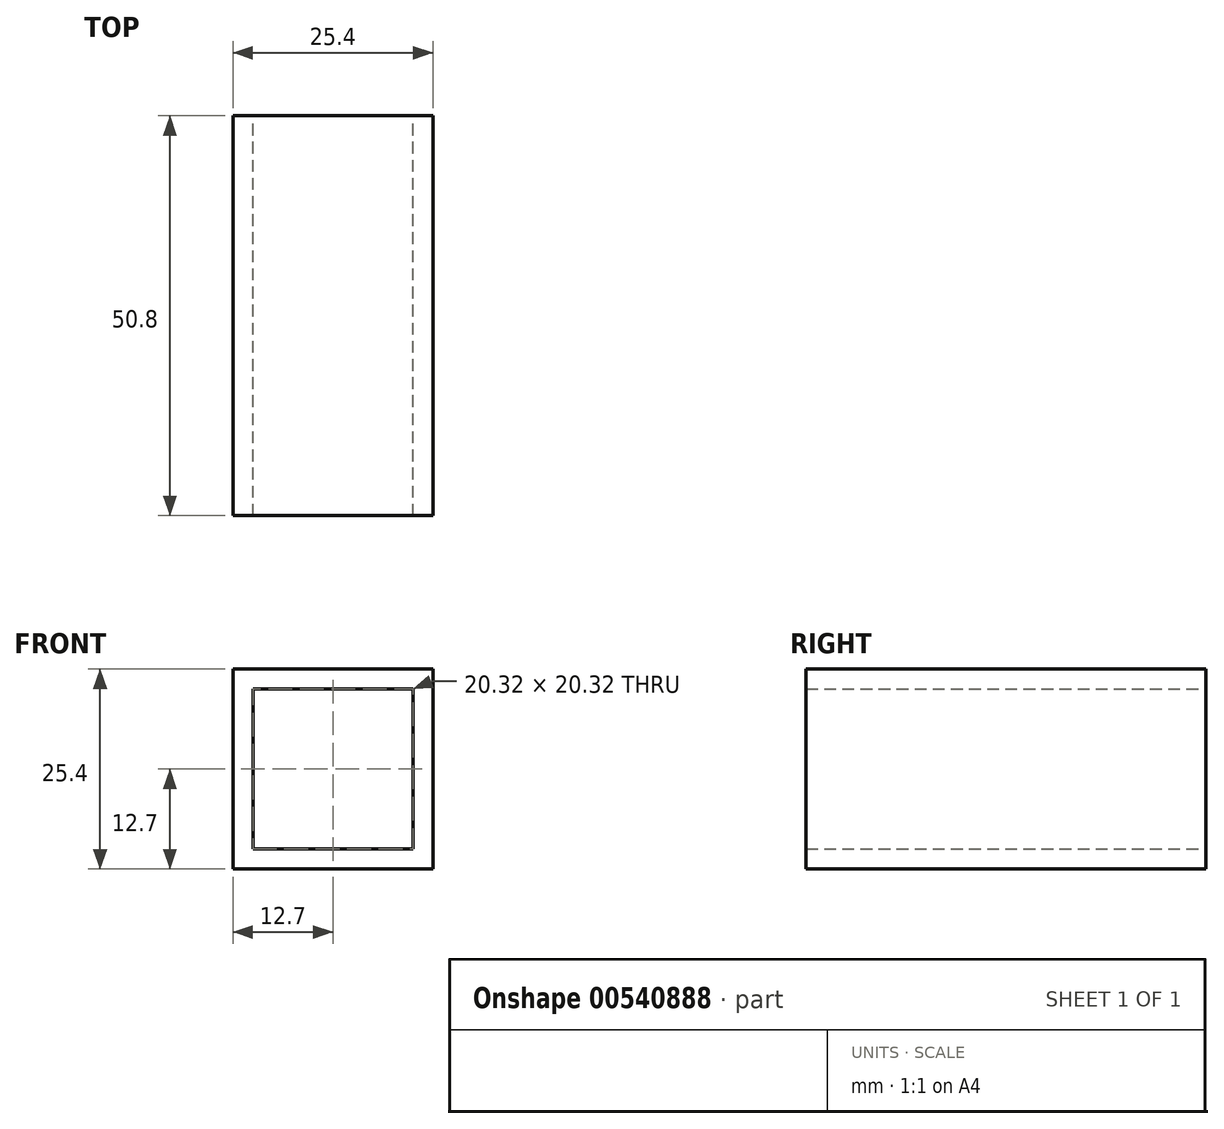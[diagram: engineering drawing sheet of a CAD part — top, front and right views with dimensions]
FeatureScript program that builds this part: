
annotation { "Feature Type Name" : "Feature", "Feature Type Description" : "" }
export const myFeature = defineFeature(function(context is Context, id is Id, definition is map)
    precondition{}
    {
        {
            var Q0;
            Q0=qCreatedBy(makeId("Front.planeOp"),FACE);
            var sketch = newSketch(context, id + "F0", { "sketchPlane" : qUnion([Q0])});
            skLineSegment(sketch, "E0.bottom", {"start": v(12.7, -12.7) * mm, "end": v(-12.7, -12.7) * mm});
            skLineSegment(sketch, "E0.top", {"start": v(12.7, 12.7) * mm, "end": v(-12.7, 12.7) * mm});
            skLineSegment(sketch, "E0.left", {"start": v(12.7, -12.7) * mm, "end": v(12.7, 12.7) * mm});
            skLineSegment(sketch, "E0.right", {"start": v(-12.7, -12.7) * mm, "end": v(-12.7, 12.7) * mm});
            skPoint(sketch, "E0.middle", {"position": v(0, 0) * mm});
            skLineSegment(sketch, "E1.bottom", {"start": v(10.16, -10.16) * mm, "end": v(-10.16, -10.16) * mm});
            skLineSegment(sketch, "E1.top", {"start": v(10.16, 10.16) * mm, "end": v(-10.16, 10.16) * mm});
            skLineSegment(sketch, "E1.left", {"start": v(10.16, -10.16) * mm, "end": v(10.16, 10.16) * mm});
            skLineSegment(sketch, "E1.right", {"start": v(-10.16, -10.16) * mm, "end": v(-10.16, 10.16) * mm});
            skSolve(sketch);
        }
        {
            var Q0;
            Q0=sQuery(id+"F0.wireOp",EDGE,"E1.top");
            extrude(context, id + "F1", {"bodyType" : ToolBodyType.SURFACE, "surfaceEntities" : qUnion([Q0]), "depth" : 50.8 * mm, "offsetDistance" : 25.4 * mm});
        }
        {
            var Q0;
            Q0 = qSketchRegion(id + "F0", true);
            extrude(context, id + "F2", {"entities" : qUnion([Q0]), "depth" : 50.8 * mm, "offsetDistance" : 25.4 * mm});
        }
    });
